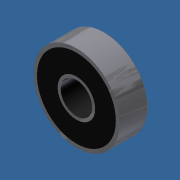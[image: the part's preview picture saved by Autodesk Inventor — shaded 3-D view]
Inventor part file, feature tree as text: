
AUTODESK INVENTOR PART (.ipt)
format: ipt  version: 2012 SP1 (Build 160190100, 190)  size: 97,792 bytes
history: native  units: in
note: dims shown in document units (in); Inventor stores cm internally (conversion verified against a paired STEP export)
features: extrude x2, sketch x2
ambient origin geometry x8: Origin, YZ Plane, XZ Plane, XY Plane, X Axis, Y Axis, Z Axis, Center Point
bodies: Solid1 (feature_tree)
feature tree (4):
  extrude  "Extrusion1"  Depth=0.8661in
  extrude  "Extrusion2"  Depth=0.0004in TaperAngle=0.0deg
  sketch  "Sketch1"  dims[d0=0.315in d1=0.8661in]
  sketch  "Sketch2"  dims[d2=0.2756in d3=0.0in d4=0.0004in d5=0.0in]
